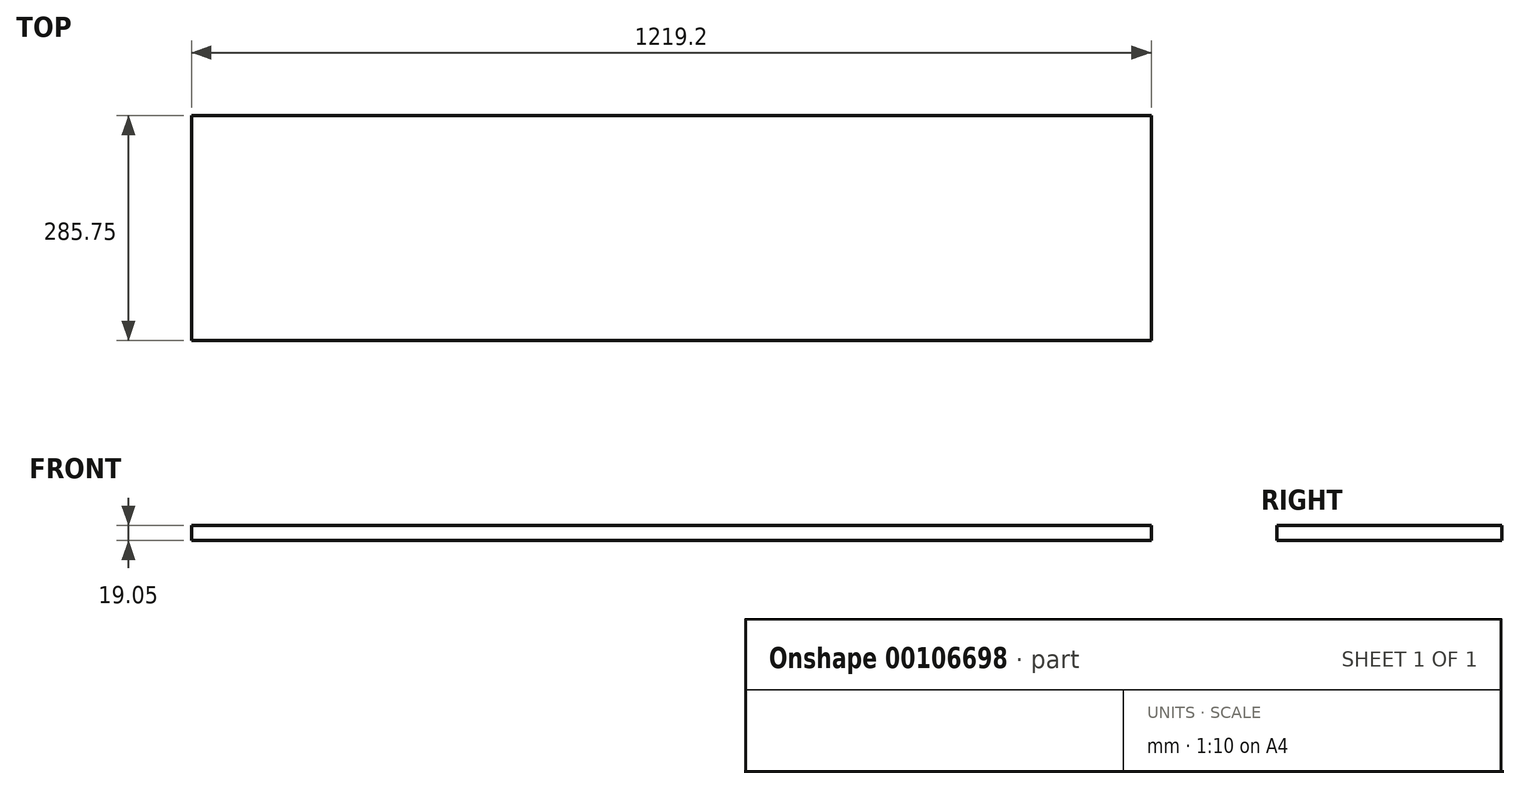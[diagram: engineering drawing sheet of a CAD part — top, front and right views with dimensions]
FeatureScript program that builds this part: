
annotation { "Feature Type Name" : "Feature", "Feature Type Description" : "" }
export const myFeature = defineFeature(function(context is Context, id is Id, definition is map)
    precondition{}
    {
        {
            var Q0;
            Q0=qCreatedBy(makeId("Top.planeOp"),FACE);
            var sketch = newSketch(context, id + "F0", { "sketchPlane" : qUnion([Q0])});
            skLineSegment(sketch, "E0.bottom", {"start": v(0, 0) * mm, "end": v(1219.2, 0) * mm});
            skLineSegment(sketch, "E0.top", {"start": v(0, 285.75) * mm, "end": v(1219.2, 285.75) * mm});
            skLineSegment(sketch, "E0.left", {"start": v(0, 0) * mm, "end": v(0, 285.75) * mm});
            skLineSegment(sketch, "E0.right", {"start": v(1219.2, 0) * mm, "end": v(1219.2, 285.75) * mm});
            skSolve(sketch);
        }
        {
            var Q0;
            Q0=makeQuery(id+"F0.imprint","IMPRINT",FACE,{"disambiguationData":[TD([[makeQuery(id+"F0.imprint","IMPRINT",EDGE,{"derivedFrom":sQuery(id+"F0.wireOp",EDGE,"E0.bottom")}),1.0]])]});
            extrude(context, id + "F1", {"entities" : qUnion([Q0]), "depth" : 19.05 * mm});
        }
    });
